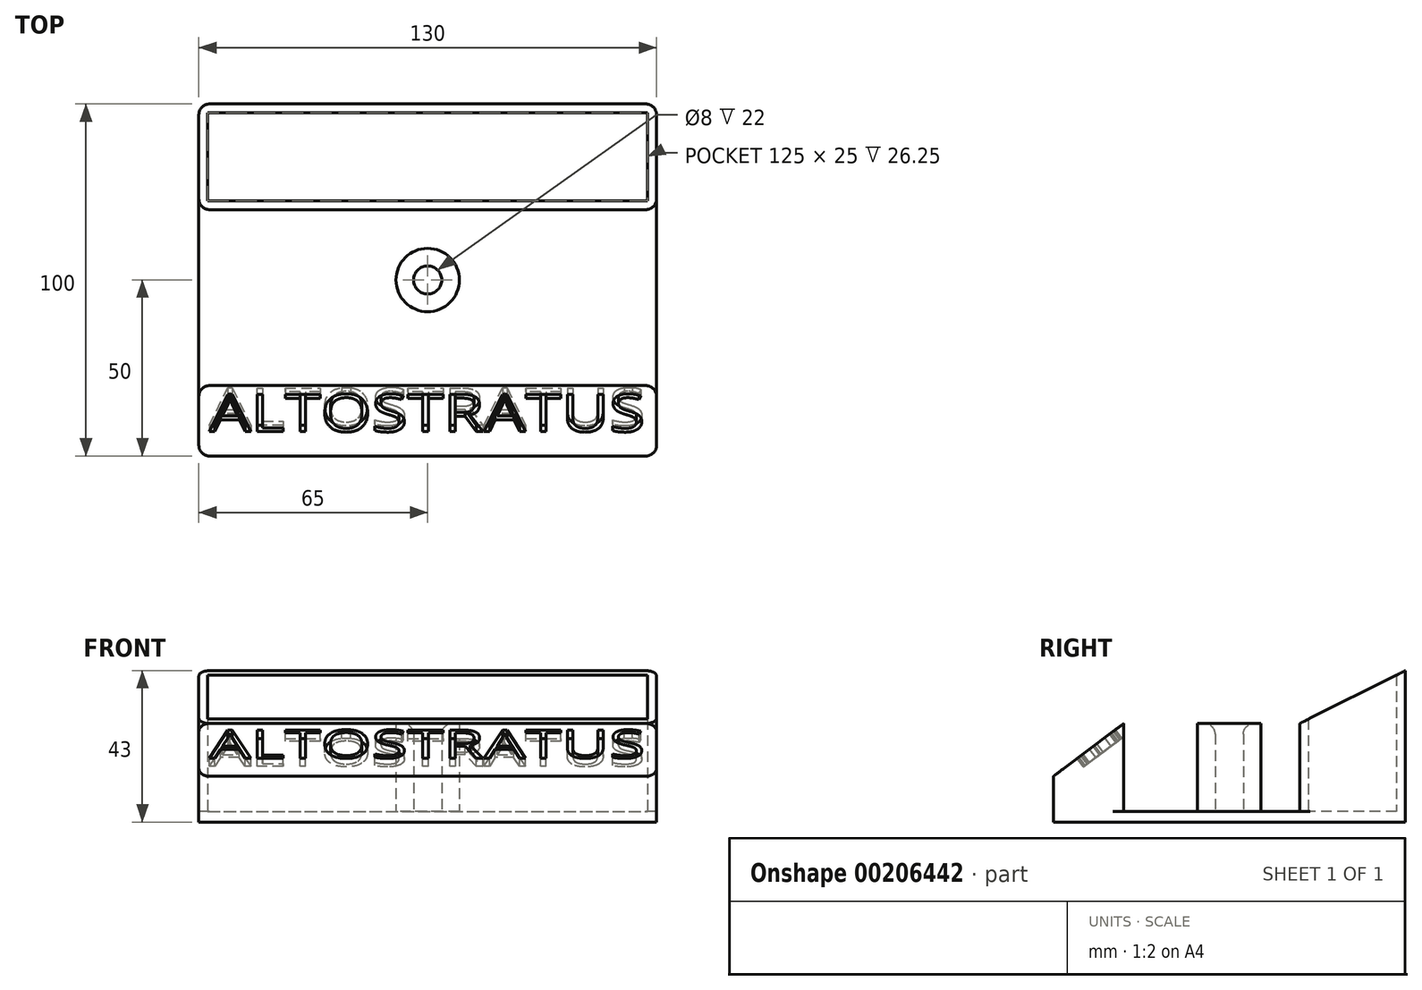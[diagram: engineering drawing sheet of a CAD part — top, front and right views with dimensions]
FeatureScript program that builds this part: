
annotation { "Feature Type Name" : "Feature", "Feature Type Description" : "" }
export const myFeature = defineFeature(function(context is Context, id is Id, definition is map)
    precondition{}
    {
        {
            var Q0;
            Q0=qCreatedBy(makeId("Top.planeOp"),FACE);
            var sketch = newSketch(context, id + "F0", { "sketchPlane" : qUnion([Q0])});
            skLineSegment(sketch, "E0.bottom", {"start": v(-65, 100) * mm, "end": v(65, 100) * mm});
            skLineSegment(sketch, "E0.top", {"start": v(-65, 0) * mm, "end": v(65, 0) * mm});
            skLineSegment(sketch, "E0.left", {"start": v(65, 100) * mm, "end": v(65, 0) * mm});
            skLineSegment(sketch, "E0.right", {"start": v(-65, 100) * mm, "end": v(-65, 0) * mm});
            skSolve(sketch);
        }
        {
            var Q0;
            Q0=makeQuery(id+"F0.imprint","IMPRINT",FACE,{"disambiguationData":[TD([[makeQuery(id+"F0.imprint","IMPRINT",EDGE,{"derivedFrom":sQuery(id+"F0.wireOp",EDGE,"E0.bottom")}),-1.0]])]});
            extrude(context, id + "F1", {"entities" : qUnion([Q0]), "depth" : 3 * mm});
        }
        {
            var Q0;
            Q0=makeQuery(id+"F1.opExtrude","CAP_FACE",FACE,{"disambiguationData":[OSD([sQuery(id+"F0.wireOp",EDGE,"E0.bottom"),sQuery(id+"F0.wireOp",EDGE,"E0.top"),sQuery(id+"F0.wireOp",EDGE,"E0.left"),sQuery(id+"F0.wireOp",EDGE,"E0.right")])],"isStart":false});
            var sketch = newSketch(context, id + "F2", { "sketchPlane" : qUnion([Q0])});
            skLineSegment(sketch, "E1", {"start": v(0, 0) * mm, "end": v(0, 100) * mm, "construction": true});
            skCircle(sketch, "E2", {"center": v(0, 50) * mm, "radius": 9 * mm});
            skCircle(sketch, "E3", {"center": v(0, 50) * mm, "radius": 4 * mm});
            skLineSegment(sketch, "E4.bottom", {"start": v(-65, 0) * mm, "end": v(65, 0) * mm});
            skLineSegment(sketch, "E4.top", {"start": v(-65, 20) * mm, "end": v(65, 20) * mm});
            skLineSegment(sketch, "E4.left", {"start": v(-65, 0) * mm, "end": v(-65, 20) * mm});
            skLineSegment(sketch, "E4.right", {"start": v(65, 0) * mm, "end": v(65, 20) * mm});
            skLineSegment(sketch, "E5.bottom", {"start": v(-65, 100) * mm, "end": v(65, 100) * mm});
            skLineSegment(sketch, "E5.top", {"start": v(-65, 70) * mm, "end": v(65, 70) * mm});
            skLineSegment(sketch, "E5.left", {"start": v(-65, 100) * mm, "end": v(-65, 70) * mm});
            skLineSegment(sketch, "E5.right", {"start": v(65, 100) * mm, "end": v(65, 70) * mm});
            skLineSegment(sketch, "E6.0", {"start": v(62.5, 97.5) * mm, "end": v(62.5, 72.5) * mm});
            skLineSegment(sketch, "E6.1", {"start": v(-62.5, 97.5) * mm, "end": v(62.5, 97.5) * mm});
            skLineSegment(sketch, "E6.2", {"start": v(-62.5, 97.5) * mm, "end": v(-62.5, 72.5) * mm});
            skLineSegment(sketch, "E6.3", {"start": v(-62.5, 72.5) * mm, "end": v(62.5, 72.5) * mm});
            skSolve(sketch);
        }
        {
            var Q0;
            Q0=makeQuery(id+"F2.imprint","IMPRINT",FACE,{"disambiguationData":[TD([[makeQuery(id+"F2.imprint","IMPRINT",EDGE,{"derivedFrom":sQuery(id+"F2.wireOp",EDGE,"E5.bottom")}),-1.0]])]});
            extrude(context, id + "F3", {"entities" : qUnion([Q0]), "operationType" : NewBodyOperationType.ADD, "depth" : 40 * mm});
        }
        {
            var Q0;
            Q0=makeQuery(id+"F2.imprint","IMPRINT",FACE,{"disambiguationData":[TD([[makeQuery(id+"F2.imprint","IMPRINT",EDGE,{"derivedFrom":sQuery(id+"F2.wireOp",EDGE,"E2")}),1.0]])]});
            var Q1;
            Q1=makeQuery(id+"F2.imprint","IMPRINT",FACE,{"disambiguationData":[TD([[makeQuery(id+"F2.imprint","IMPRINT",EDGE,{"derivedFrom":sQuery(id+"F2.wireOp",EDGE,"E4.bottom")}),1.0]])]});
            extrude(context, id + "F4", {"entities" : qUnion([Q0, Q1]), "operationType" : NewBodyOperationType.ADD, "depth" : 25 * mm});
        }
        {
            var Q0;
            Q0=makeQuery(id+"F4.opExtrude","CAP_EDGE",EDGE,{"disambiguationData":[OSD([sQuery(id+"F2.wireOp",EDGE,"E4.bottom")])],"isStart":false});
            chamfer(context, id + "F5", {"entities" : qUnion([Q0]), "chamferType" : ChamferType.TWO_OFFSETS, "width1" : 20 * mm, "oppositeDirection" : false, "width2" : 15 * mm, "tangentPropagation" : true});
        }
        {
            var Q0;
            Q0=makeQuery(id+"F3.opExtrude","CAP_EDGE",EDGE,{"disambiguationData":[OSD([sQuery(id+"F2.wireOp",EDGE,"E5.top")])],"isStart":false});
            chamfer(context, id + "F6", {"entities" : qUnion([Q0]), "chamferType" : ChamferType.TWO_OFFSETS, "width1" : 30 * mm, "oppositeDirection" : false, "width2" : 15 * mm, "tangentPropagation" : true});
        }
        {
            var Q0;
            Q0=makeQuery(id+"F3.boolean.opBoolean","MERGE",EDGE,{"derivedFrom":[makeQuery(id+"F1.opExtrude","SWEPT_EDGE",EDGE,{"disambiguationData":[OSD([sQuery(id+"F0.wireOp",EDGE,"E0.bottom"),sQuery(id+"F0.wireOp",EDGE,"E0.right")])]}),makeQuery(id+"F3.opExtrude","SWEPT_EDGE",EDGE,{"disambiguationData":[OSD([sQuery(id+"F2.wireOp",EDGE,"E5.bottom"),sQuery(id+"F2.wireOp",EDGE,"E5.left")])]})]});
            var Q1;
            Q1=makeQuery(id+"F3.opExtrude","SWEPT_EDGE",EDGE,{"disambiguationData":[OSD([sQuery(id+"F0.wireOp",EDGE,"E0.right"),sQuery(id+"F2.wireOp",EDGE,"E5.top"),sQuery(id+"F2.wireOp",EDGE,"E5.left")])]});
            var Q2;
            Q2=makeQuery(id+"F3.opExtrude","SWEPT_EDGE",EDGE,{"disambiguationData":[OSD([sQuery(id+"F0.wireOp",EDGE,"E0.left"),sQuery(id+"F2.wireOp",EDGE,"E5.top"),sQuery(id+"F2.wireOp",EDGE,"E5.right")])]});
            var Q3;
            Q3=makeQuery(id+"F4.boolean.opBoolean","MERGE",EDGE,{"derivedFrom":[makeQuery(id+"F1.opExtrude","SWEPT_EDGE",EDGE,{"disambiguationData":[OSD([sQuery(id+"F0.wireOp",EDGE,"E0.top"),sQuery(id+"F0.wireOp",EDGE,"E0.right")])]}),makeQuery(id+"F4.opExtrude","SWEPT_EDGE",EDGE,{"disambiguationData":[OSD([sQuery(id+"F2.wireOp",EDGE,"E4.bottom"),sQuery(id+"F2.wireOp",EDGE,"E4.left")])]})]});
            var Q4;
            Q4=makeQuery(id+"F3.boolean.opBoolean","MERGE",EDGE,{"derivedFrom":[makeQuery(id+"F1.opExtrude","SWEPT_EDGE",EDGE,{"disambiguationData":[OSD([sQuery(id+"F0.wireOp",EDGE,"E0.bottom"),sQuery(id+"F0.wireOp",EDGE,"E0.left")])]}),makeQuery(id+"F3.opExtrude","SWEPT_EDGE",EDGE,{"disambiguationData":[OSD([sQuery(id+"F2.wireOp",EDGE,"E5.bottom"),sQuery(id+"F2.wireOp",EDGE,"E5.right")])]})]});
            var Q5;
            Q5=makeQuery(id+"F4.boolean.opBoolean","MERGE",EDGE,{"derivedFrom":[makeQuery(id+"F1.opExtrude","SWEPT_EDGE",EDGE,{"disambiguationData":[OSD([sQuery(id+"F0.wireOp",EDGE,"E0.top"),sQuery(id+"F0.wireOp",EDGE,"E0.left")])]}),makeQuery(id+"F4.opExtrude","SWEPT_EDGE",EDGE,{"disambiguationData":[OSD([sQuery(id+"F2.wireOp",EDGE,"E4.bottom"),sQuery(id+"F2.wireOp",EDGE,"E4.right")])]})]});
            var Q6;
            Q6=makeQuery(id+"F4.opExtrude","SWEPT_EDGE",EDGE,{"disambiguationData":[OSD([sQuery(id+"F0.wireOp",EDGE,"E0.left"),sQuery(id+"F2.wireOp",EDGE,"E4.top"),sQuery(id+"F2.wireOp",EDGE,"E4.right")])]});
            var Q7;
            Q7=makeQuery(id+"F4.opExtrude","SWEPT_EDGE",EDGE,{"disambiguationData":[OSD([sQuery(id+"F0.wireOp",EDGE,"E0.right"),sQuery(id+"F2.wireOp",EDGE,"E4.top"),sQuery(id+"F2.wireOp",EDGE,"E4.left")])]});
            var Q8;
            Q8=makeQuery(id+"F4.opExtrude","CAP_EDGE",EDGE,{"disambiguationData":[OSD([sQuery(id+"F2.wireOp",EDGE,"E3")])],"isStart":false});
            fillet(context, id + "F7", {"entities" : qUnion([Q0, Q1, Q2, Q3, Q4, Q5, Q6, Q7, Q8]), "radius" : 3 * mm, "tangentPropagation" : true, "allowEdgeOverflow" : false});
        }
        {
            var Q0;
            Q0=makeQuery(id+"F5.opChamfer","BLEND_FACE",FACE,{"disambiguationData":[OSD([sQuery(id+"F2.wireOp",EDGE,"E4.bottom")])]});
            var sketch = newSketch(context, id + "F8", { "sketchPlane" : qUnion([Q0])});
            skLineSegment(sketch, "E7.0", {"start": v(62, 10.8) * mm, "end": v(-62, 10.8) * mm});
            skLineSegment(sketch, "E8.0", {"start": v(-62, 29.8) * mm, "end": v(62, 29.8) * mm});
            skText(sketch, "E9", { "text": "ALTOSTRATUS", "fontName": "OpenSans-Regular.ttf"});
            skLineSegment(sketch, "E10", {"start": v(-62, 10.8) * mm, "end": v(-62, 47.82) * mm});
            skLineSegment(sketch, "E11", {"start": v(62, 10.8) * mm, "end": v(62, 49.07) * mm});
            skPoint(sketch, "E11.endSnap0", {"position": v(62, 15.3) * mm});
            const initialGuessF8  = {"E9": [-0.062, 0.01644, 1, 0, 0.01336]};
            skSetInitialGuess(sketch, initialGuessF8);
            skSolve(sketch);
        }
        {
            var Q0;
            Q0=makeQuery(id+"F8.imprint","IMPRINT",FACE,{"disambiguationData":[TD([[makeQuery(id+"F8.imprint","IMPRINT",EDGE,{"derivedFrom":sQuery(id+"F8.wireOp",EDGE,"E9.sketch_text.stroke-0")}),-1.0]])]});
            var Q1;
            Q1=makeQuery(id+"F8.imprint","IMPRINT",FACE,{"disambiguationData":[TD([[makeQuery(id+"F8.imprint","IMPRINT",EDGE,{"derivedFrom":sQuery(id+"F8.wireOp",EDGE,"E9.sketch_text.stroke-13")}),-1.0]])]});
            var Q2;
            Q2=makeQuery(id+"F8.imprint","IMPRINT",FACE,{"disambiguationData":[TD([[makeQuery(id+"F8.imprint","IMPRINT",EDGE,{"derivedFrom":sQuery(id+"F8.wireOp",EDGE,"E9.sketch_text.stroke-19")}),-1.0]])]});
            var Q3;
            Q3=makeQuery(id+"F8.imprint","IMPRINT",FACE,{"disambiguationData":[TD([[makeQuery(id+"F8.imprint","IMPRINT",EDGE,{"derivedFrom":sQuery(id+"F8.wireOp",EDGE,"E9.sketch_text.stroke-27")}),-1.0]])]});
            var Q4;
            Q4=makeQuery(id+"F8.imprint","IMPRINT",FACE,{"disambiguationData":[TD([[makeQuery(id+"F8.imprint","IMPRINT",EDGE,{"derivedFrom":sQuery(id+"F8.wireOp",EDGE,"E9.sketch_text.stroke-43")}),-1.0]])]});
            var Q5;
            Q5=makeQuery(id+"F8.imprint","IMPRINT",FACE,{"disambiguationData":[TD([[makeQuery(id+"F8.imprint","IMPRINT",EDGE,{"derivedFrom":sQuery(id+"F8.wireOp",EDGE,"E9.sketch_text.stroke-58")}),-1.0]])]});
            var Q6;
            Q6=makeQuery(id+"F8.imprint","IMPRINT",FACE,{"disambiguationData":[TD([[makeQuery(id+"F8.imprint","IMPRINT",EDGE,{"derivedFrom":sQuery(id+"F8.wireOp",EDGE,"E9.sketch_text.stroke-72")}),-1.0]])]});
            var Q7;
            Q7=makeQuery(id+"F8.imprint","IMPRINT",FACE,{"disambiguationData":[TD([[makeQuery(id+"F8.imprint","IMPRINT",EDGE,{"derivedFrom":sQuery(id+"F8.wireOp",EDGE,"E9.sketch_text.stroke-90")}),-1.0]])]});
            var Q8;
            Q8=makeQuery(id+"F8.imprint","IMPRINT",FACE,{"disambiguationData":[TD([[makeQuery(id+"F8.imprint","IMPRINT",EDGE,{"derivedFrom":sQuery(id+"F8.wireOp",EDGE,"E9.sketch_text.stroke-104")}),-1.0]])]});
            var Q9;
            Q9=makeQuery(id+"F8.imprint","IMPRINT",FACE,{"disambiguationData":[TD([[makeQuery(id+"F8.imprint","IMPRINT",EDGE,{"derivedFrom":sQuery(id+"F8.wireOp",EDGE,"E9.sketch_text.stroke-110")}),-1.0]])]});
            var Q10;
            Q10=makeQuery(id+"F8.imprint","IMPRINT",FACE,{"disambiguationData":[TD([[makeQuery(id+"F8.imprint","IMPRINT",EDGE,{"derivedFrom":sQuery(id+"F8.wireOp",EDGE,"E9.sketch_text.stroke-124")}),-1.0]])]});
            var Q11;
            Q11=makeQuery(id+"F8.imprint","IMPRINT",FACE,{"disambiguationData":[TD([[makeQuery(id+"F8.imprint","IMPRINT",EDGE,{"derivedFrom":sQuery(id+"F8.wireOp",EDGE,"E9.sketch_text.stroke-129")}),-1.0]])]});
            extrude(context, id + "F9", {"entities" : qUnion([Q0, Q1, Q2, Q3, Q4, Q5, Q6, Q7, Q8, Q9, Q10, Q11]), "operationType" : NewBodyOperationType.REMOVE, "oppositeDirection" : true, "depth" : 3 * mm});
        }
    });
